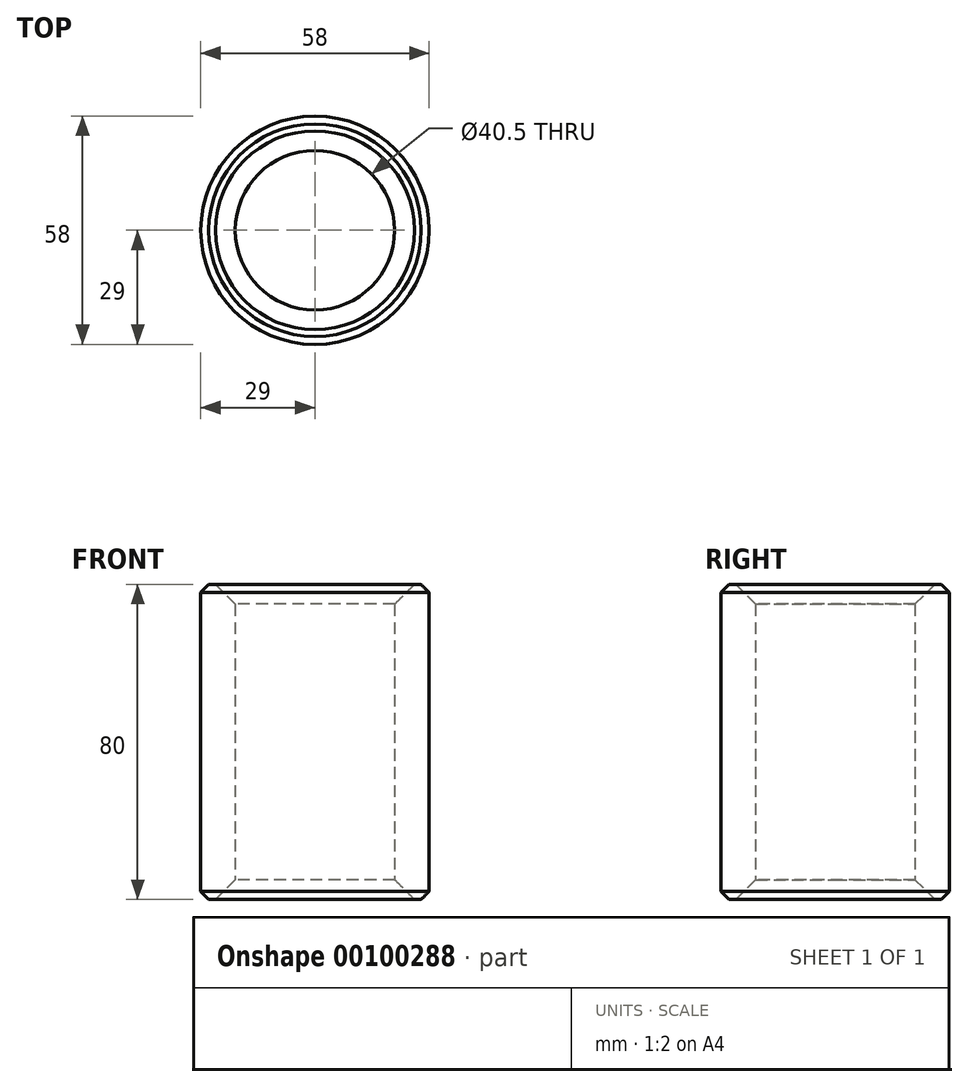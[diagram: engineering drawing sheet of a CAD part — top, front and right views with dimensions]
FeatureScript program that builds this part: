
annotation { "Feature Type Name" : "Feature", "Feature Type Description" : "" }
export const myFeature = defineFeature(function(context is Context, id is Id, definition is map)
    precondition{}
    {
        {
            var Q0;
            Q0=qCreatedBy(makeId("Top.planeOp"),FACE);
            var sketch = newSketch(context, id + "F0", { "sketchPlane" : qUnion([Q0])});
            skCircle(sketch, "E0", {"center": v(0, 0) * mm, "radius": 29 * mm});
            skCircle(sketch, "E1", {"center": v(0, 0) * mm, "radius": 20.25 * mm});
            skSolve(sketch);
        }
        {
            var Q0;
            Q0 = qSketchRegion(id + "F0", true);
            extrude(context, id + "F1", {"entities" : qUnion([Q0]), "endBound" : BoundingType.SYMMETRIC, "depth" : 80 * mm});
        }
        {
            var Q0;
            Q0=makeQuery(id+"F1.opExtrude","CAP_EDGE",EDGE,{"disambiguationData":[OSD([sQuery(id+"F0.wireOp",EDGE,"E1")])],"isStart":false});
            chamfer(context, id + "F2", {"entities" : qUnion([Q0]), "width" : 5 * mm, "tangentPropagation" : true});
        }
        {
            var Q0;
            Q0=makeQuery(id+"F1.opExtrude","CAP_EDGE",EDGE,{"disambiguationData":[OSD([sQuery(id+"F0.wireOp",EDGE,"E0")])],"isStart":true});
            chamfer(context, id + "F3", {"entities" : qUnion([Q0]), "width" : 2 * mm, "tangentPropagation" : true});
        }
        {
            var Q0;
            Q0=makeQuery(id+"F1.opExtrude","CAP_EDGE",EDGE,{"disambiguationData":[OSD([sQuery(id+"F0.wireOp",EDGE,"E0")])],"isStart":false});
            chamfer(context, id + "F4", {"entities" : qUnion([Q0]), "width" : 2 * mm, "tangentPropagation" : true});
        }
        {
            var Q0;
            Q0=makeQuery(id+"F1.opExtrude","CAP_EDGE",EDGE,{"disambiguationData":[OSD([sQuery(id+"F0.wireOp",EDGE,"E1")])],"isStart":true});
            chamfer(context, id + "F5", {"entities" : qUnion([Q0]), "width" : 5 * mm, "tangentPropagation" : true});
        }
    });
